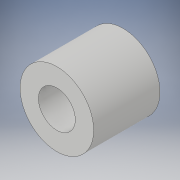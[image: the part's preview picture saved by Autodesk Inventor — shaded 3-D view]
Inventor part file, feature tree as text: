
AUTODESK INVENTOR PART (.ipt)
format: ipt  version: 2019 (Build 230136000, 136)  size: 96,768 bytes
history: native  units: in
note: dims shown in document units (in); Inventor stores cm internally (conversion verified against a paired STEP export)
features: extrude x1, sketch x1
ambient origin geometry x8: Origin, YZ Plane, XZ Plane, XY Plane, X Axis, Y Axis, Z Axis, Center Point
bodies: Solid1 (feature_tree)
feature tree (2):
  extrude  "Extrusion1"  Depth=0.45in
  sketch  "Sketch1"  dims[d0=0.25in d1=0.5in d2=0.45in d3=0.0in]
